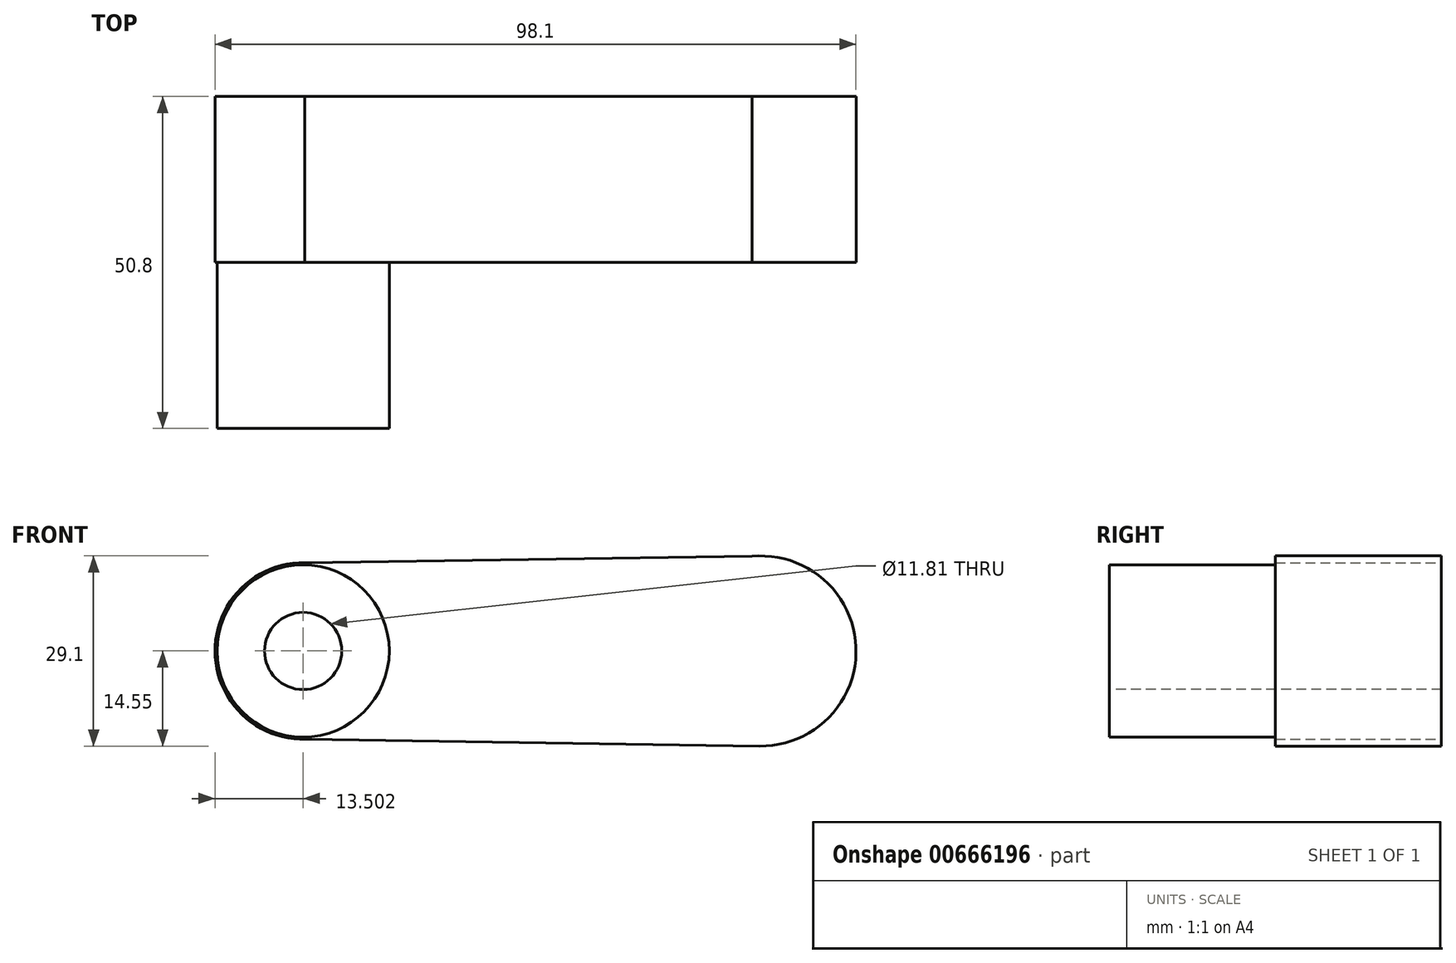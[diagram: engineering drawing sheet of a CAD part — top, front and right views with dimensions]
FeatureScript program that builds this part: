
annotation { "Feature Type Name" : "Feature", "Feature Type Description" : "" }
export const myFeature = defineFeature(function(context is Context, id is Id, definition is map)
    precondition{}
    {
        {
            var Q0;
            Q0=qCreatedBy(makeId("Front.planeOp"),FACE);
            var sketch = newSketch(context, id + "F0", { "sketchPlane" : qUnion([Q0])});
            skCircle(sketch, "E0", {"center": v(-37.15, 0) * mm, "radius": 13.5 * mm});
            skCircle(sketch, "E1", {"center": v(32.9, 0) * mm, "radius": 14.55 * mm});
            skLineSegment(sketch, "E2", {"start": v(-37.78, 13.48) * mm, "end": v(33.87, 14.51) * mm});
            skLineSegment(sketch, "E3", {"start": v(-36.77, -13.5) * mm, "end": v(32.69, -14.55) * mm});
            skSolve(sketch);
        }
        {
            var Q0;
            {var subQ0=sQuery(id+"F0.wireOp",EDGE,"E2");var subQ1=sQuery(id+"F0.wireOp",EDGE,"E0");var subQ2=makeQuery(id+"F0.imprint","INTERSECT",VERTEX,{"disambiguationData":[OD(0.0)],"derivedFrom":[subQ1,subQ0]});Q0=makeQuery(id+"F0.imprint","IMPRINT",FACE,{"disambiguationData":[TD([[makeQuery(id+"F0.imprint","IMPRINT",EDGE,{"disambiguationData":[TD([[subQ2,1.0]])],"derivedFrom":subQ1}),1.0]])]});}
            var Q1;
            {var subQ0=sQuery(id+"F0.wireOp",EDGE,"E2");var subQ1=sQuery(id+"F0.wireOp",EDGE,"E1");var subQ2=makeQuery(id+"F0.imprint","INTERSECT",VERTEX,{"disambiguationData":[OD(0.0)],"derivedFrom":[subQ1,subQ0]});Q1=makeQuery(id+"F0.imprint","IMPRINT",FACE,{"disambiguationData":[TD([[makeQuery(id+"F0.imprint","IMPRINT",EDGE,{"disambiguationData":[TD([[subQ2,-1.0]])],"derivedFrom":subQ1}),1.0]])]});}
            var Q2;
            {var subQ0=sQuery(id+"F0.wireOp",EDGE,"E2");var subQ1=sQuery(id+"F0.wireOp",EDGE,"E0");var subQ2=makeQuery(id+"F0.imprint","INTERSECT",VERTEX,{"disambiguationData":[OD(0.0)],"derivedFrom":[subQ1,subQ0]});Q2=makeQuery(id+"F0.imprint","IMPRINT",FACE,{"disambiguationData":[TD([[makeQuery(id+"F0.imprint","IMPRINT",EDGE,{"disambiguationData":[TD([[subQ2,-1.0]])],"derivedFrom":subQ1}),1.0]])]});}
            var Q3;
            {var subQ0=sQuery(id+"F0.wireOp",EDGE,"E1");var subQ1=makeQuery(id+"F0.imprint","INTERSECT",VERTEX,{"derivedFrom":[subQ0,sQuery(id+"F0.wireOp",EDGE,"E3")]});Q3=makeQuery(id+"F0.imprint","IMPRINT",FACE,{"disambiguationData":[TD([[makeQuery(id+"F0.imprint","IMPRINT",EDGE,{"disambiguationData":[TD([[subQ1,1.0]])],"derivedFrom":subQ0}),1.0]])]});}
            var Q4;
            {var subQ0=sQuery(id+"F0.wireOp",EDGE,"E3");Q4=makeQuery(id+"F0.imprint","IMPRINT",FACE,{"disambiguationData":[TD([[makeQuery(id+"F0.imprint","IMPRINT",EDGE,{"derivedFrom":subQ0}),1.0]])]});}
            extrude(context, id + "F1", {"entities" : qUnion([Q0, Q1, Q2, Q3, Q4]), "depth" : 25.4 * mm, "offsetDistance" : 25.4 * mm});
        }
        {
            var Q0;
            Q0=makeQuery(id+"F1.opExtrude","CAP_FACE",FACE,{"disambiguationData":[OSD([sQuery(id+"F0.wireOp",EDGE,"E0"),sQuery(id+"F0.wireOp",EDGE,"E1"),sQuery(id+"F0.wireOp",EDGE,"E2"),sQuery(id+"F0.wireOp",EDGE,"E3")])],"isStart":false});
            var sketch = newSketch(context, id + "F2", { "sketchPlane" : qUnion([Q0])});
            skCircle(sketch, "E4", {"center": v(-37.15, 0) * mm, "radius": 13.17 * mm});
            skSolve(sketch);
        }
        {
            var Q0;
            Q0=makeQuery(id+"F2.imprint","IMPRINT",FACE,{"disambiguationData":[TD([[makeQuery(id+"F2.imprint","IMPRINT",EDGE,{"derivedFrom":sQuery(id+"F2.wireOp",EDGE,"E4")}),1.0]])]});
            extrude(context, id + "F3", {"entities" : qUnion([Q0]), "operationType" : NewBodyOperationType.ADD, "depth" : 25.4 * mm, "offsetDistance" : 25.4 * mm});
        }
        {
            var Q0;
            Q0=makeQuery(id+"F3.opExtrude","CAP_FACE",FACE,{"disambiguationData":[OSD([sQuery(id+"F2.wireOp",EDGE,"E4")])],"isStart":false});
            var sketch = newSketch(context, id + "F4", { "sketchPlane" : qUnion([Q0])});
            skCircle(sketch, "E5", {"center": v(-37.15, 0) * mm, "radius": 5.9 * mm});
            skSolve(sketch);
        }
        {
            var Q0;
            Q0=makeQuery(id+"F4.imprint","IMPRINT",FACE,{"disambiguationData":[TD([[makeQuery(id+"F4.imprint","IMPRINT",EDGE,{"derivedFrom":sQuery(id+"F4.wireOp",EDGE,"E5")}),1.0]])]});
            extrude(context, id + "F5", {"entities" : qUnion([Q0]), "operationType" : NewBodyOperationType.REMOVE, "oppositeDirection" : true, "depth" : 127 * mm, "offsetDistance" : 25.4 * mm});
        }
    });
